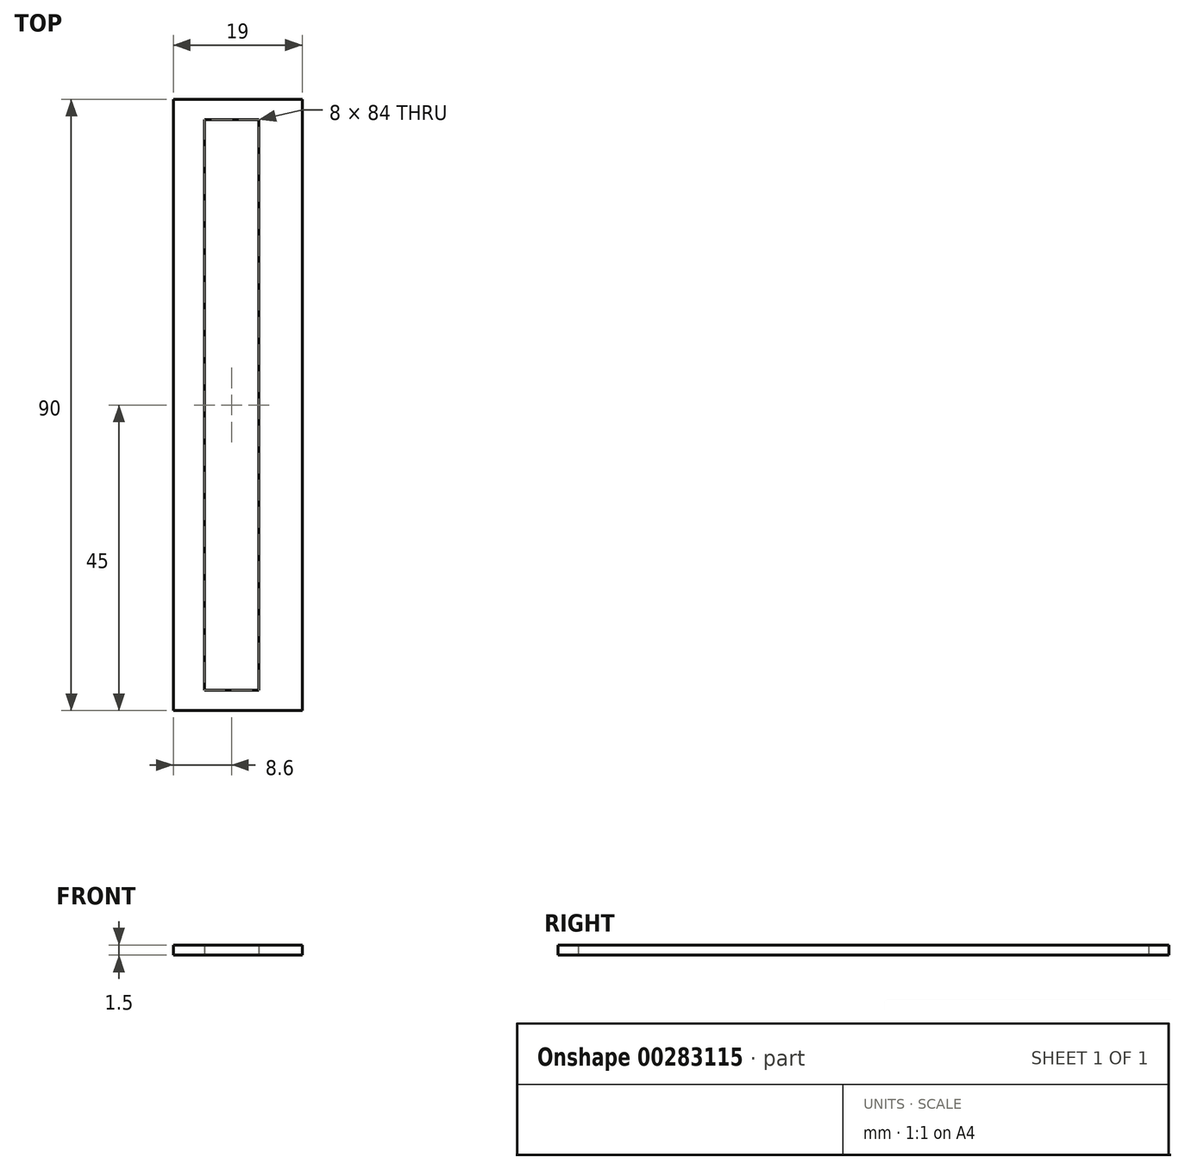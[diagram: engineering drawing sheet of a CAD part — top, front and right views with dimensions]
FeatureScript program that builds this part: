
annotation { "Feature Type Name" : "Feature", "Feature Type Description" : "" }
export const myFeature = defineFeature(function(context is Context, id is Id, definition is map)
    precondition{}
    {
        {
            var Q0;
            Q0=qCreatedBy(makeId("Top.planeOp"),FACE);
            var sketch = newSketch(context, id + "F0", { "sketchPlane" : qUnion([Q0])});
            skLineSegment(sketch, "E0.bottom", {"start": v(-4, 42) * mm, "end": v(4, 42) * mm});
            skLineSegment(sketch, "E0.top", {"start": v(-4, -42) * mm, "end": v(4, -42) * mm});
            skLineSegment(sketch, "E0.left", {"start": v(-4, 42) * mm, "end": v(-4, -42) * mm});
            skLineSegment(sketch, "E0.right", {"start": v(4, 42) * mm, "end": v(4, -42) * mm});
            skPoint(sketch, "E0.middle", {"position": v(0, 0) * mm});
            skLineSegment(sketch, "E1.bottom", {"start": v(-8.6, 45) * mm, "end": v(10.4, 45) * mm});
            skLineSegment(sketch, "E1.top", {"start": v(-8.6, -45) * mm, "end": v(10.4, -45) * mm});
            skLineSegment(sketch, "E1.left", {"start": v(-8.6, 45) * mm, "end": v(-8.6, -45) * mm});
            skLineSegment(sketch, "E1.right", {"start": v(10.4, 45) * mm, "end": v(10.4, -45) * mm});
            skSolve(sketch);
        }
        {
            var Q0;
            Q0=makeQuery(id+"F0.imprint","IMPRINT",FACE,{"disambiguationData":[TD([[makeQuery(id+"F0.imprint","IMPRINT",EDGE,{"derivedFrom":sQuery(id+"F0.wireOp",EDGE,"E0.bottom")}),1.0]])]});
            extrude(context, id + "F1", {"entities" : qUnion([Q0]), "depth" : 1.5 * mm});
        }
    });
